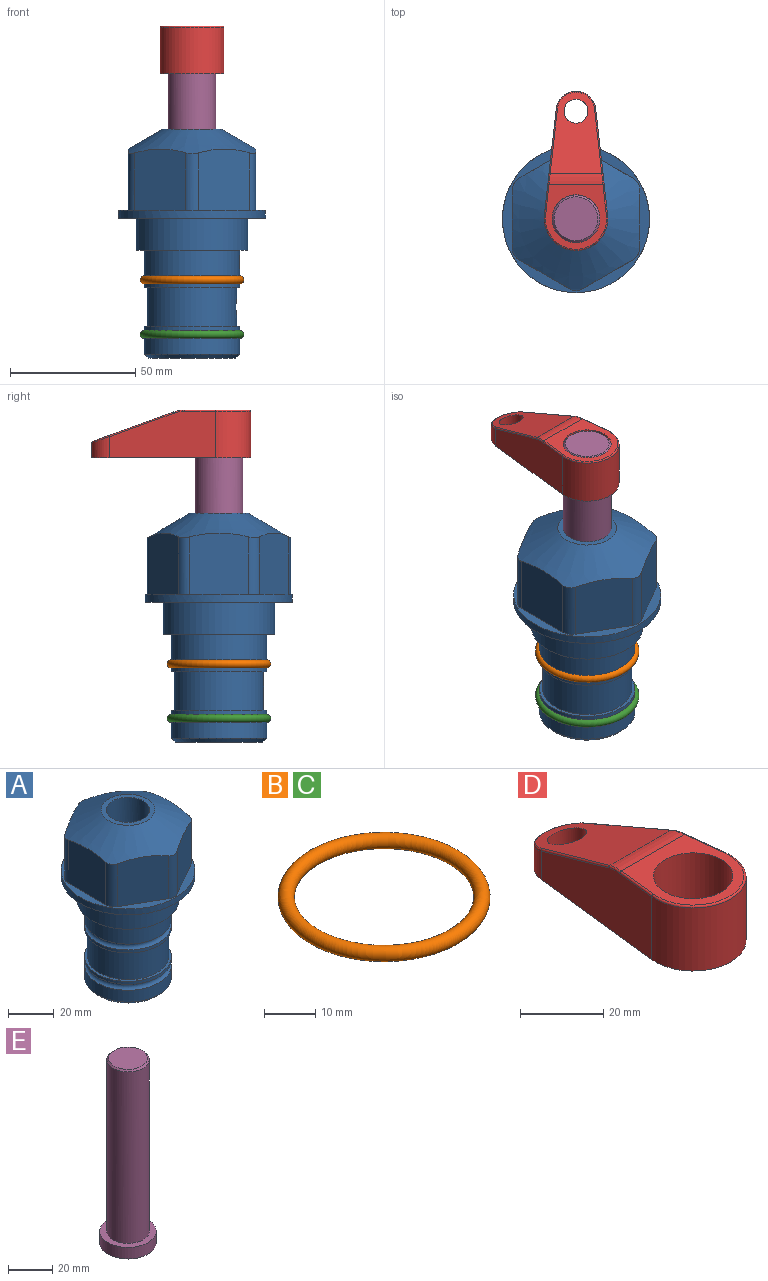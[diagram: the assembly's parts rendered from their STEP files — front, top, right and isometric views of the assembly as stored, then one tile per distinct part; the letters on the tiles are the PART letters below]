
ASSEMBLY  parts=5 mates=3
PART A: 36 faces, bbox 58.7x58.7x91.2 mm
  f0: cylinder r=17.78mm len=35.56mm, axis (0,0,1), area 1670.8mm2, adj f23,f24,f31
  f1: cylinder r=19.05mm len=38.1mm, axis (0,0,1), area 1191.9mm2, adj f26,f27,f30
  f2: plane 58.66x58.66mm, normal (0,0,-1), area 1150.6mm2, adj f3,f28
  f3: cylinder r=29.33mm len=58.66mm, axis (0,0,-1), area 585.1mm2, adj f2,f4
  f4: plane 58.66x58.66mm, normal (0,0,1), area 475.9mm2, adj f3,f5,f6,f7,f8,f9,f10,f11
  f5: plane 24.5x20.32mm, normal (-0.5,0.87,0), area 562.8mm2, adj f4,f15,f16,f17
  f6: plane 24.5x20.32mm, normal (0.5,0.87,0), area 562.8mm2, adj f4,f14,f15,f17
  f7: plane 24.5x23.48mm, normal (1,0,0), area 562.8mm2, adj f4,f13,f14,f17
  f8: plane 24.5x20.32mm, normal (0.5,-0.87,0), area 562.8mm2, adj f4,f12,f13,f17
  f9: plane 24.5x20.32mm, normal (-0.5,-0.87,0), area 562.8mm2, adj f4,f11,f12,f17
  f10: plane 24.5x23.48mm, normal (-1,0,0), area 562.8mm2, adj f4,f11,f16,f17
  f11: cylinder r=5.08mm len=23.01mm, axis (0,0,-1), area 121.2mm2, adj f4,f9,f10,f17
  f12: cylinder r=5.08mm len=23.01mm, axis (0,0,-1), area 121.2mm2, adj f4,f8,f9,f17
  f13: cylinder r=5.08mm len=23.01mm, axis (0,0,-1), area 121.2mm2, adj f4,f7,f8,f17
  f14: cylinder r=5.08mm len=23.01mm, axis (0,0,-1), area 121.2mm2, adj f4,f6,f7,f17
  f15: cylinder r=5.08mm len=23.01mm, axis (0,0,-1), area 121.2mm2, adj f4,f5,f6,f17
  f16: cylinder r=5.08mm len=23.01mm, axis (0,0,-1), area 121.2mm2, adj f4,f5,f10,f17
  f17: cone r=11.73mm half-angle=60deg, axis (0,0,-1), area 2071.8mm2, adj f5,f6,f7,f8,f9,f10,f11,f12
  f18: plane 23.46x23.46mm, normal (0,0,1), area 147.4mm2, adj f17,f35
  f19: plane 34.93x34.93mm, normal (0,0,-1), area 958mm2, adj f29
  f20: cylinder r=19.05mm len=38.1mm, axis (0,0,1), area 760.1mm2, adj f21,f29
  f21: torus R=19.05mm, axis (0,0,1), area 565.3mm2, adj f20,f22
  f22: cylinder r=19.05mm len=38.1mm, axis (0,0,1), area 190mm2, adj f21,f23
  f23: plane 38.1x38.1mm, normal (0,0,1), area 146.9mm2, adj f0,f22
  f24: plane 38.1x38.1mm, normal (0,0,-1), area 146.9mm2, adj f0,f25
  f25: cylinder r=19.05mm len=38.1mm, axis (0,0,1), area 190mm2, adj f24,f26
  f26: torus R=19.05mm, axis (0,0,1), area 565.3mm2, adj f1,f25
  f27: plane 44.45x44.45mm, normal (0,0,-1), area 411.7mm2, adj f1,f28
  f28: cylinder r=22.23mm len=44.45mm, axis (0,0,1), area 1773.5mm2, adj f2,f27
  f29: cone r=19.05mm half-angle=45deg, axis (0,0,1), area 257.5mm2, adj f19,f20
  f30: cylinder r=3.17mm len=6.75mm, axis (-1,0,0), area 128mm2, adj f1,f33
  f31: cylinder r=3.17mm len=6.35mm, axis (-1,0,0), area 102.5mm2, adj f0,f33
  f32: plane 25.4x25.4mm, normal (0,0,1), area 506.7mm2, adj f33
  f33: cylinder r=12.7mm len=66.42mm, axis (0,0,-1), area 5236.2mm2, adj f30,f31,f32,f34
  f34: cone r=9.53mm half-angle=30deg, axis (0,0,-1), area 443.4mm2, adj f33,f35
  f35: cylinder r=9.53mm len=19.05mm, axis (0,0,-1), area 849mm2, adj f18,f34
PART B: 1 faces, bbox 44.7x44.7x3.2 mm
  f0: torus R=19.05mm, axis (0,0,1), area 1193.9mm2
PART C: same geometry as B
PART D: 44 faces, bbox 27.5x64.5x19.1 mm
  f0: plane 2.3x0.95mm, normal (0,0,-1), area 1mm2, adj f25,f30,f34
  f1: plane 63.5x25.4mm, normal (0,0,-1), area 561.7mm2, adj f2,f3,f4,f5,f6,f7,f19,f20
  f2: cylinder r=12.7mm len=25.4mm, axis (0,0,-1), area 792.2mm2, adj f1,f3,f5,f13
  f3: plane 42.33x18.54mm, normal (0.99,0.11,0), area 647mm2, adj f1,f2,f4,f11,f12,f14
  f4: cylinder r=7.94mm len=15.78mm, axis (0,0,-1), area 158.6mm2, adj f1,f3,f5,f16
  f5: plane 42.33x18.54mm, normal (-0.99,0.11,0), area 647mm2, adj f1,f2,f4,f15,f17,f18
  f6: cylinder r=9.53mm len=19.05mm, axis (0,0,-1), area 1140.1mm2, adj f1,f8
  f7: cylinder r=4.76mm len=10.98mm, axis (0,0,-1), area 276.1mm2, adj f1,f9
  f8: plane 25.83x24.38mm, normal (0,0,1), area 262.2mm2, adj f6,f10,f11,f13,f15
  f9: plane 32.49x20.55mm, normal (0,0.34,0.94), area 489.9mm2, adj f7,f10,f14,f16,f18
  f10: cylinder r=12.7mm len=21.49mm, axis (-1,0,0), area 93.2mm2, adj f8,f9,f12,f17
  f11: cylinder r=0.51mm len=12.34mm, axis (0.11,-0.99,0), area 9.9mm2, adj f3,f8,f12,f13
  f12: bspline ~7.62x1.64mm, area 3.5mm2, adj f3,f10,f11,f14
  f13: torus R=12.19mm, axis (0,0,1), area 33.6mm2, adj f2,f8,f11,f15
  f14: cylinder r=0.51mm len=26.01mm, axis (0.1,-0.93,0.34), area 21.6mm2, adj f3,f9,f12,f16
  f15: cylinder r=0.51mm len=12.34mm, axis (0.11,0.99,0), area 9.9mm2, adj f5,f8,f13,f17
  f16: bspline ~15.78x7.05mm, area 15.7mm2, adj f4,f9,f14,f18
  f17: bspline ~7.62x1.64mm, area 3.5mm2, adj f5,f10,f15,f18
  f18: cylinder r=0.51mm len=26.01mm, axis (0.1,0.93,-0.34), area 21.6mm2, adj f5,f9,f16,f17
  f19: plane 21.6x14.29mm, normal (-0.99,-0.11,0), area 242.6mm2, adj f1,f26,f28,f34,f36,f38
  f20: plane 21.6x14.29mm, normal (0.99,-0.11,0), area 242.6mm2, adj f1,f27,f29,f37,f39,f41
  f21: cylinder r=12.7mm len=14.29mm, axis (0,0,-1), area 173.2mm2, adj f1,f26,f27,f30,f31,f33
  f22: cylinder r=7.94mm len=7.63mm, axis (0,0,-1), area 53.8mm2, adj f1,f28,f29,f42
  f23: plane 2.3x0.95mm, normal (0,0,-1), area 1mm2, adj f25,f33,f37
  f24: plane 17.94x12.32mm, normal (0,-0.34,-0.94), area 191.2mm2, adj f25,f38,f41,f42
  f25: cylinder r=9.53mm len=12.93mm, axis (-1,0,0), area 37.5mm2, adj f0,f23,f24,f31,f36,f39
  f26: cylinder r=1.59mm len=14.29mm, axis (0,0,-1), area 49mm2, adj f1,f19,f21,f32
  f27: cylinder r=1.59mm len=14.29mm, axis (0,0,-1), area 49mm2, adj f1,f20,f21,f35
  f28: cylinder r=1.59mm len=7.28mm, axis (0,0,-1), area 22.1mm2, adj f1,f19,f22,f40
  f29: cylinder r=1.59mm len=7.28mm, axis (0,0,-1), area 22.1mm2, adj f1,f20,f22,f43
  f30: torus R=14.29mm, axis (0,0,1), area 5.8mm2, adj f0,f21,f31,f32
  f31: bspline ~11.06x2.73mm, area 20.8mm2, adj f21,f25,f30,f33
  f32: sphere r=1.59mm, area 5.4mm2, adj f26,f30,f34
  f33: torus R=14.29mm, axis (0,0,1), area 5.8mm2, adj f21,f23,f31,f35
  f34: cylinder r=1.59mm len=1.68mm, axis (-0.11,0.99,0), area 2.4mm2, adj f0,f19,f32,f36
  f35: sphere r=1.59mm, area 5.4mm2, adj f27,f33,f37
  f36: bspline ~5.82x2.33mm, area 7.7mm2, adj f19,f25,f34,f38
  f37: cylinder r=1.59mm len=1.68mm, axis (0.11,0.99,0), area 2.4mm2, adj f20,f23,f35,f39
  f38: cylinder r=1.59mm len=18.33mm, axis (0.1,-0.93,0.34), area 46.7mm2, adj f19,f24,f36,f40
  f39: bspline ~5.82x2.33mm, area 7.7mm2, adj f20,f25,f37,f41
  f40: sphere r=1.59mm, area 3.6mm2, adj f28,f38,f42
  f41: cylinder r=1.59mm len=18.33mm, axis (0.1,0.93,-0.34), area 46.7mm2, adj f20,f24,f39,f43
  f42: bspline ~8.31x1.84mm, area 15.3mm2, adj f22,f24,f40,f43
  f43: sphere r=1.59mm, area 3.6mm2, adj f29,f41,f42
PART E: 6 faces, bbox 25.4x25.4x101.6 mm
  f0: plane 17.46x17.46mm, normal (0,0,1), area 239.5mm2, adj f5
  f1: plane 25.4x25.4mm, normal (0,0,-1), area 506.7mm2, adj f2
  f2: cylinder r=12.7mm len=25.4mm, axis (0,0,1), area 506.7mm2, adj f1,f3
  f3: plane 25.4x25.4mm, normal (0,0,1), area 221.7mm2, adj f2,f4
  f4: cylinder r=9.53mm len=94.46mm, axis (0,0,1), area 5653mm2, adj f3,f5
  f5: cone r=8.73mm half-angle=45deg, axis (0,0,-1), area 64.4mm2, adj f0,f4
PLACE A at identity fixed
PLACE B at identity
PLACE C t=(0,0,-21.72)mm
PLACE D t=(0,0,57.67)mm
PLACE E t=(0,0,3.06)mm
MATE fastened E.f2 <-> D.f2  axis (0,0,1) through (0,0,76.72)mm
MATE fastened A.f0 <-> A.f0  axis (0,0,1) through (0,0,-47.69)mm
MATE cylindrical E.f2 <-> A.f0  axis (0,0,1) through (0,0,28.7)mm
